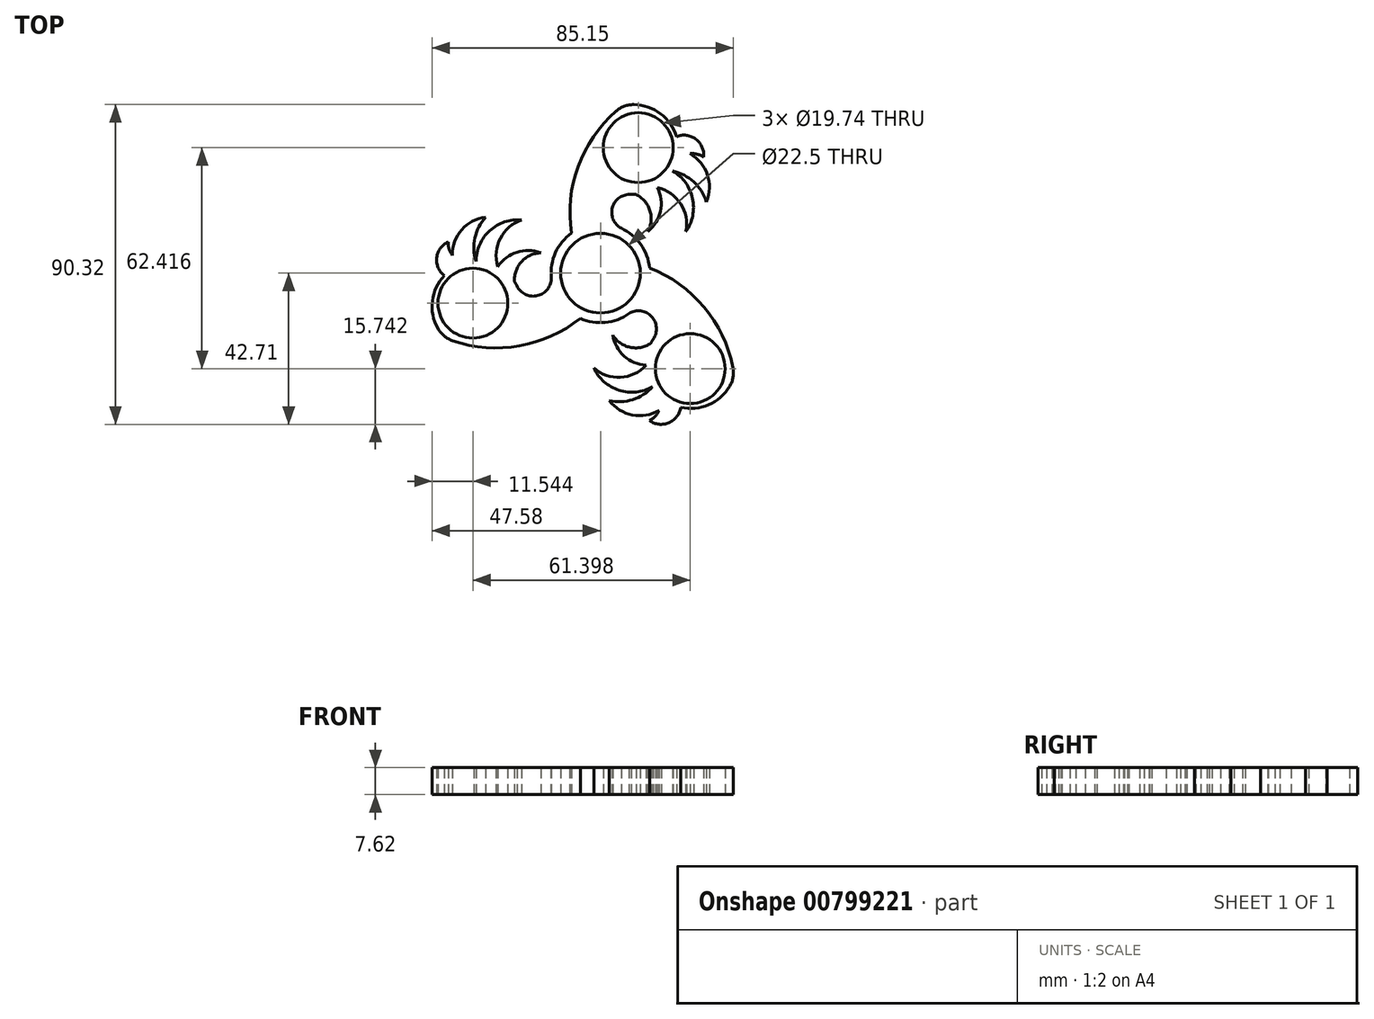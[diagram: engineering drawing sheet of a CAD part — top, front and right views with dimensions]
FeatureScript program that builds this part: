
annotation { "Feature Type Name" : "Feature", "Feature Type Description" : "" }
export const myFeature = defineFeature(function(context is Context, id is Id, definition is map)
    precondition{}
    {
        {
            var Q0;
            Q0=qCreatedBy(makeId("Top.planeOp"),FACE);
            var sketch = newSketch(context, id + "F0", { "sketchPlane" : qUnion([Q0])});
            skCircle(sketch, "E0", {"center": v(0, 0) * mm, "radius": 13.97 * mm});
            skCircle(sketch, "E1", {"center": v(0, 0) * mm, "radius": 11.25 * mm});
            skArc(sketch, "E2", {"start": v(6.16, 47.21) * mm, "mid": v(-5.92, 31.22) * mm, "end": v(-8.2, 11.3) * mm});
            skArc(sketch, "E3", {"start": v(8.66, 22.23) * mm, "mid": v(3.38, 18.59) * mm, "end": v(5.87, 12.68) * mm});
            skArc(sketch, "E4", {"start": v(8.66, 22.23) * mm, "mid": v(21.94, 36.17) * mm, "end": v(6.16, 47.21) * mm});
            skArc(sketch, "E5", {"start": v(13.38, 11.73) * mm, "mid": v(13.96, 17.7) * mm, "end": v(10.05, 22.23) * mm});
            skArc(sketch, "E6", {"start": v(13.38, 11.73) * mm, "mid": v(16.93, 17.48) * mm, "end": v(16.1, 24.18) * mm});
            skArc(sketch, "E7", {"start": v(24.13, 11.73) * mm, "mid": v(22.66, 19.6) * mm, "end": v(16.1, 24.18) * mm});
            skArc(sketch, "E8", {"start": v(24.13, 11.73) * mm, "mid": v(26.03, 21.08) * mm, "end": v(20.44, 28.8) * mm});
            skArc(sketch, "E9", {"start": v(29.93, 20.15) * mm, "mid": v(26.36, 25.77) * mm, "end": v(20.44, 28.8) * mm});
            skArc(sketch, "E10", {"start": v(29.93, 20.15) * mm, "mid": v(29.5, 29.45) * mm, "end": v(22, 34.96) * mm});
            skArc(sketch, "E11", {"start": v(29.15, 32.85) * mm, "mid": v(26.92, 37.87) * mm, "end": v(21.46, 38.58) * mm});
            skArc(sketch, "E12", {"start": v(29.15, 32.85) * mm, "mid": v(25.33, 33.77) * mm, "end": v(21.72, 32.23) * mm});
            skArc(sketch, "E13.1.0", {"start": v(-32.41, 15.84) * mm, "mid": v(-40.25, 10.82) * mm, "end": v(-41.28, 1.57) * mm});
            skArc(sketch, "E13.1.1", {"start": v(-22.22, 15.03) * mm, "mid": v(-31.27, 12) * mm, "end": v(-35.17, 3.3) * mm});
            skArc(sketch, "E13.1.2", {"start": v(-43.97, -18.27) * mm, "mid": v(-24.08, -20.73) * mm, "end": v(-5.69, -12.76) * mm});
            skArc(sketch, "E13.1.3", {"start": v(-32.41, 15.84) * mm, "mid": v(-35.5, 9.95) * mm, "end": v(-35.17, 3.3) * mm});
            skArc(sketch, "E13.1.4", {"start": v(-23.58, -3.61) * mm, "mid": v(-17.79, -6.37) * mm, "end": v(-13.91, -1.26) * mm});
            skArc(sketch, "E13.1.5", {"start": v(-43.03, 8.82) * mm, "mid": v(-46.26, 4.37) * mm, "end": v(-44.14, -0.7) * mm});
            skArc(sketch, "E13.1.6", {"start": v(-22.22, 15.03) * mm, "mid": v(-28.3, 9.82) * mm, "end": v(-28.99, 1.85) * mm});
            skArc(sketch, "E13.1.7", {"start": v(-23.58, -3.61) * mm, "mid": v(-42.3, 0.91) * mm, "end": v(-43.97, -18.27) * mm});
            skArc(sketch, "E13.1.8", {"start": v(-43.03, 8.82) * mm, "mid": v(-41.9, 5.06) * mm, "end": v(-38.77, 2.7) * mm});
            skArc(sketch, "E13.1.9", {"start": v(-16.85, 5.72) * mm, "mid": v(-23.6, 5.93) * mm, "end": v(-28.99, 1.85) * mm});
            skArc(sketch, "E13.1.10", {"start": v(-16.85, 5.72) * mm, "mid": v(-22.3, 3.24) * mm, "end": v(-24.28, -2.41) * mm});
            skArc(sketch, "E13.2.0", {"start": v(2.49, -36) * mm, "mid": v(10.75, -40.27) * mm, "end": v(19.28, -36.54) * mm});
            skArc(sketch, "E13.2.1", {"start": v(-1.9, -26.76) * mm, "mid": v(5.24, -33.08) * mm, "end": v(14.73, -32.1) * mm});
            skArc(sketch, "E13.2.2", {"start": v(37.8, -28.94) * mm, "mid": v(30, -10.48) * mm, "end": v(13.9, 1.45) * mm});
            skArc(sketch, "E13.2.3", {"start": v(2.49, -36) * mm, "mid": v(9.13, -35.71) * mm, "end": v(14.73, -32.1) * mm});
            skArc(sketch, "E13.2.4", {"start": v(14.92, -18.61) * mm, "mid": v(14.4, -12.22) * mm, "end": v(8.05, -11.42) * mm});
            skArc(sketch, "E13.2.5", {"start": v(13.87, -41.67) * mm, "mid": v(19.34, -42.25) * mm, "end": v(22.68, -37.87) * mm});
            skArc(sketch, "E13.2.6", {"start": v(-1.9, -26.76) * mm, "mid": v(5.64, -29.43) * mm, "end": v(12.9, -26.03) * mm});
            skArc(sketch, "E13.2.7", {"start": v(14.92, -18.61) * mm, "mid": v(20.36, -37.09) * mm, "end": v(37.8, -28.94) * mm});
            skArc(sketch, "E13.2.8", {"start": v(13.87, -41.67) * mm, "mid": v(16.58, -38.82) * mm, "end": v(17.06, -34.92) * mm});
            skArc(sketch, "E13.2.9", {"start": v(3.47, -17.46) * mm, "mid": v(6.67, -23.4) * mm, "end": v(12.9, -26.03) * mm});
            skArc(sketch, "E13.2.10", {"start": v(3.47, -17.46) * mm, "mid": v(8.34, -20.94) * mm, "end": v(14.23, -19.82) * mm});
            skCircle(sketch, "E14", {"center": v(10.67, 35.45) * mm, "radius": 9.87 * mm});
            skCircle(sketch, "E15.1.0", {"center": v(-36.04, -8.48) * mm, "radius": 9.87 * mm});
            skCircle(sketch, "E15.2.0", {"center": v(25.36, -26.97) * mm, "radius": 9.87 * mm});
            skSolve(sketch);
        }
        {
            var Q0;
            {var subQ3=sQuery(id+"F0.wireOp",EDGE,"E13.1.2");Q0=makeQuery(id+"F0.imprint","IMPRINT",FACE,{"disambiguationData":[TD([[makeQuery(id+"F0.imprint","IMPRINT",EDGE,{"derivedFrom":subQ3}),1.0]])]});}
            var Q1;
            Q1=makeQuery(id+"F0.imprint","IMPRINT",FACE,{"disambiguationData":[TD([[makeQuery(id+"F0.imprint","IMPRINT",EDGE,{"derivedFrom":sQuery(id+"F0.wireOp",EDGE,"E1")}),-1.0]])]});
            var Q2;
            {var subQ5=sQuery(id+"F0.wireOp",EDGE,"E13.1.5");Q2=makeQuery(id+"F0.imprint","IMPRINT",FACE,{"disambiguationData":[TD([[makeQuery(id+"F0.imprint","IMPRINT",EDGE,{"derivedFrom":subQ5}),1.0]])]});}
            var Q3;
            {var subQ0=sQuery(id+"F0.wireOp",EDGE,"E13.1.3");Q3=makeQuery(id+"F0.imprint","IMPRINT",FACE,{"disambiguationData":[TD([[makeQuery(id+"F0.imprint","IMPRINT",EDGE,{"derivedFrom":subQ0}),-1.0]])]});}
            var Q4;
            {var subQ0=sQuery(id+"F0.wireOp",EDGE,"E13.1.7");var subQ1=sQuery(id+"F0.wireOp",EDGE,"E13.1.0");var subQ2=makeQuery(id+"F0.imprint","INTERSECT",VERTEX,{"derivedFrom":[subQ1,subQ0]});Q4=makeQuery(id+"F0.imprint","IMPRINT",FACE,{"disambiguationData":[TD([[makeQuery(id+"F0.imprint","IMPRINT",EDGE,{"disambiguationData":[TD([[subQ2,1.0]])],"derivedFrom":subQ1}),1.0]])]});}
            var Q5;
            {var subQ0=sQuery(id+"F0.wireOp",EDGE,"E13.1.1");Q5=makeQuery(id+"F0.imprint","IMPRINT",FACE,{"disambiguationData":[TD([[makeQuery(id+"F0.imprint","IMPRINT",EDGE,{"derivedFrom":subQ0}),1.0]])]});}
            var Q6;
            {var subQ0=sQuery(id+"F0.wireOp",EDGE,"E13.1.9");Q6=makeQuery(id+"F0.imprint","IMPRINT",FACE,{"disambiguationData":[TD([[makeQuery(id+"F0.imprint","IMPRINT",EDGE,{"derivedFrom":subQ0}),1.0]])]});}
            var Q7;
            {var subQ3=sQuery(id+"F0.wireOp",EDGE,"E2");Q7=makeQuery(id+"F0.imprint","IMPRINT",FACE,{"disambiguationData":[TD([[makeQuery(id+"F0.imprint","IMPRINT",EDGE,{"derivedFrom":subQ3}),1.0]])]});}
            var Q8;
            {var subQ3=sQuery(id+"F0.wireOp",EDGE,"E13.2.2");Q8=makeQuery(id+"F0.imprint","IMPRINT",FACE,{"disambiguationData":[TD([[makeQuery(id+"F0.imprint","IMPRINT",EDGE,{"derivedFrom":subQ3}),1.0]])]});}
            var Q9;
            {var subQ3=sQuery(id+"F0.wireOp",EDGE,"E11");Q9=makeQuery(id+"F0.imprint","IMPRINT",FACE,{"disambiguationData":[TD([[makeQuery(id+"F0.imprint","IMPRINT",EDGE,{"derivedFrom":subQ3}),1.0]])]});}
            var Q10;
            {var subQ0=sQuery(id+"F0.wireOp",EDGE,"E9");Q10=makeQuery(id+"F0.imprint","IMPRINT",FACE,{"disambiguationData":[TD([[makeQuery(id+"F0.imprint","IMPRINT",EDGE,{"derivedFrom":subQ0}),-1.0]])]});}
            var Q11;
            {var subQ0=sQuery(id+"F0.wireOp",EDGE,"E7");Q11=makeQuery(id+"F0.imprint","IMPRINT",FACE,{"disambiguationData":[TD([[makeQuery(id+"F0.imprint","IMPRINT",EDGE,{"derivedFrom":subQ0}),-1.0]])]});}
            var Q12;
            {var subQ0=sQuery(id+"F0.wireOp",EDGE,"E5");Q12=makeQuery(id+"F0.imprint","IMPRINT",FACE,{"disambiguationData":[TD([[makeQuery(id+"F0.imprint","IMPRINT",EDGE,{"derivedFrom":subQ0}),-1.0]])]});}
            var Q13;
            {var subQ0=sQuery(id+"F0.wireOp",EDGE,"E10");var subQ1=sQuery(id+"F0.wireOp",EDGE,"E4");var subQ2=makeQuery(id+"F0.imprint","INTERSECT",VERTEX,{"derivedFrom":[subQ1,subQ0]});Q13=makeQuery(id+"F0.imprint","IMPRINT",FACE,{"disambiguationData":[TD([[makeQuery(id+"F0.imprint","IMPRINT",EDGE,{"disambiguationData":[TD([[subQ2,1.0]])],"derivedFrom":subQ1}),-1.0]])]});}
            var Q14;
            {var subQ0=sQuery(id+"F0.wireOp",EDGE,"E13.2.9");Q14=makeQuery(id+"F0.imprint","IMPRINT",FACE,{"disambiguationData":[TD([[makeQuery(id+"F0.imprint","IMPRINT",EDGE,{"derivedFrom":subQ0}),1.0]])]});}
            var Q15;
            {var subQ0=sQuery(id+"F0.wireOp",EDGE,"E13.2.1");Q15=makeQuery(id+"F0.imprint","IMPRINT",FACE,{"disambiguationData":[TD([[makeQuery(id+"F0.imprint","IMPRINT",EDGE,{"derivedFrom":subQ0}),1.0]])]});}
            var Q16;
            {var subQ5=sQuery(id+"F0.wireOp",EDGE,"E13.2.5");Q16=makeQuery(id+"F0.imprint","IMPRINT",FACE,{"disambiguationData":[TD([[makeQuery(id+"F0.imprint","IMPRINT",EDGE,{"derivedFrom":subQ5}),1.0]])]});}
            var Q17;
            {var subQ0=sQuery(id+"F0.wireOp",EDGE,"E13.2.3");Q17=makeQuery(id+"F0.imprint","IMPRINT",FACE,{"disambiguationData":[TD([[makeQuery(id+"F0.imprint","IMPRINT",EDGE,{"derivedFrom":subQ0}),-1.0]])]});}
            var Q18;
            {var subQ0=sQuery(id+"F0.wireOp",EDGE,"E13.2.7");var subQ1=sQuery(id+"F0.wireOp",EDGE,"E13.2.0");var subQ2=makeQuery(id+"F0.imprint","INTERSECT",VERTEX,{"derivedFrom":[subQ1,subQ0]});Q18=makeQuery(id+"F0.imprint","IMPRINT",FACE,{"disambiguationData":[TD([[makeQuery(id+"F0.imprint","IMPRINT",EDGE,{"disambiguationData":[TD([[subQ2,1.0]])],"derivedFrom":subQ1}),1.0]])]});}
            extrude(context, id + "F1", {"entities" : qUnion([Q0, Q1, Q2, Q3, Q4, Q5, Q6, Q7, Q8, Q9, Q10, Q11, Q12, Q13, Q14, Q15, Q16, Q17, Q18]), "depth" : 7.62 * mm, "offsetDistance" : 25.4 * mm});
        }
        {
            var Q0;
            Q0=makeQuery(id+"F1.opExtrude","SWEPT_EDGE",EDGE,{"disambiguationData":[OSD([sQuery(id+"F0.wireOp",EDGE,"E13.2.2"),sQuery(id+"F0.wireOp",EDGE,"E13.2.7")])]});
            var Q1;
            Q1=makeQuery(id+"F1.opExtrude","SWEPT_EDGE",EDGE,{"disambiguationData":[OSD([sQuery(id+"F0.wireOp",EDGE,"E2"),sQuery(id+"F0.wireOp",EDGE,"E4")])]});
            var Q2;
            Q2=makeQuery(id+"F1.opExtrude","SWEPT_EDGE",EDGE,{"disambiguationData":[OSD([sQuery(id+"F0.wireOp",EDGE,"E13.1.2"),sQuery(id+"F0.wireOp",EDGE,"E13.1.7")])]});
            fillet(context, id + "F2", {"entities" : qUnion([Q0, Q1, Q2]), "radius" : 7.62 * mm, "tangentPropagation" : true, "allowEdgeOverflow" : false});
        }
    });
